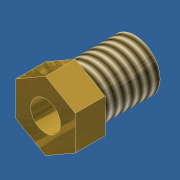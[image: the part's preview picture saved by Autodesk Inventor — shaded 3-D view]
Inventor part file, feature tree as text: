
AUTODESK INVENTOR PART (.ipt)
format: ipt  version: 2011 (Build 150239000, 239)  size: 97,792 bytes
history: native  units: in
note: dims shown in document units (in); Inventor stores cm internally (conversion verified against a paired STEP export)
features: extrude x3, sketch x3, thread x1
ambient origin geometry x8: Origin, YZ Plane, XZ Plane, XY Plane, X Axis, Y Axis, Z Axis, Center Point
bodies: Solid1 (feature_tree)
feature tree (7):
  extrude  "Extrusion1"  Depth=0.5in TaperAngle=0.0deg
  thread  "Thread1"  [1 undecoded]
  extrude  "Extrusion2"  TaperAngle=0.0deg  [1 undecoded]
  extrude  "Extrusion5"  Depth=0.25in
  sketch  "Sketch1"  dims[d0=0.425in d1=0.5in d2=0.0in d3=1.0in d4=0.0in]
  sketch  "Sketch2"  dims[d5=0.5in d6=0.0in]
  sketch  "Sketch5"  dims[d7=0.25in d8=0.0in d14=0.25in d15=1.0in d16=0.0in]
note: 2 required parameter values undecoded (feature->parameter linkage not recoverable at this tier; creation-order binding heuristic only, values carry confidence <= 0.55)
